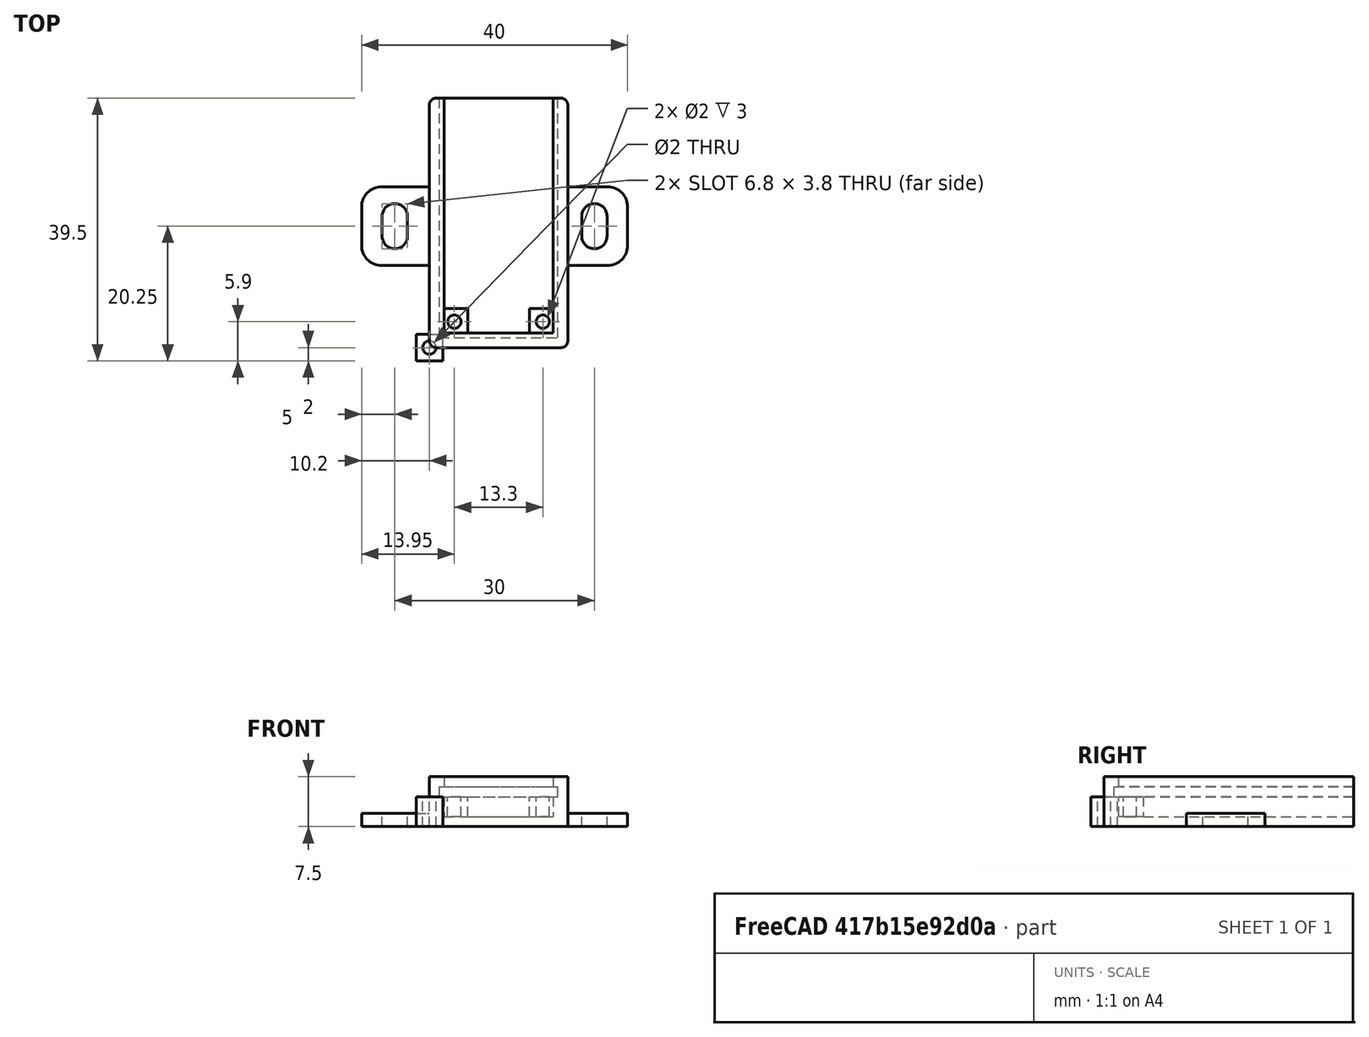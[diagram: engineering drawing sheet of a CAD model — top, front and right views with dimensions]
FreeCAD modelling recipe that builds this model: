
FCSTD DOCUMENT  (FreeCAD 0.19R23578 (Git))
Label: mosfet_d4184a_double
License: FreeArt
LicenseURL: http://artlibre.org/licence/lal
objects: Part::Box×4, Part::MultiFuse×3, Part::Cut×2, Spreadsheet::Sheet×1, Part::Fillet×1, Part::Feature×1, Part::Cylinder×1, Part::FeaturePython×1, App::Part×1
note: 12 computed .brp shape members not serialized (recipe doc carries the construction recipe); baked Part::Feature solids carry a one-line shape summary decoded from their .brp

FEATURE [Spreadsheet::Sheet] Spreadsheet  label="p"
  cells = A1=pcb_x; B1(pcb_x)=17.8; A2=pcb_y; B2(pcb_y)=36; A3=pcb_z; B3(pcb_z)=1.5; A4=pcb_under; B4(pcb_under)=3; A5=side_wall; B5(side_wall)=1.5; A6=pcb_side_lane; B6(pcb_side_lane)=0.7; A7=bottom_wall; B7(bottom_wall)=1.5; A8=pcb_above; B8(pcb_above)=1.5; A9=hole_dist_x; B9(hole_dist_x)=13.3; A10=hole_r; B10(hole_r)=1; A11=hole_off_y; B11(hole_off_y)=1.7; A12=hole_stand_size; B12(hole_stand_size)=4
FEATURE [Part::Box] Box  label="external cube"
  AttacherType = Attacher::AttachEngine3D
  Height = 7.5
  Length = 20.8
  Width = 37.5
  expr: Height = <<p>>.bottom_wall + <<p>>.pcb_under + <<p>>.pcb_z + <<p>>.pcb_above
  expr: Width = <<p>>.pcb_y + <<p>>.side_wall
  expr: Length = <<p>>.pcb_x + 2 * <<p>>.side_wall
FEATURE [Part::Box] Box006  label="internal cube"
  AttacherType = Attacher::AttachEngine3D
  Height = 6
  Length = 16.4
  Placement = pos=(2.2,2.2,1.5) rot=(0,0,1;0rad)
  Width = 36.1
  expr: .Placement.Base.y = <<p>>.side_wall + <<p>>.pcb_side_lane
  expr: .Placement.Base.x = <<p>>.side_wall + <<p>>.pcb_side_lane
  expr: .Placement.Base.z = <<p>>.bottom_wall
  expr: Height = <<p>>.pcb_under + <<p>>.pcb_z + <<p>>.pcb_above
  expr: Width = <<p>>.pcb_y - 2 * <<p>>.pcb_side_lane + <<p>>.side_wall
  expr: Length = <<p>>.pcb_x - 2 * <<p>>.pcb_side_lane
FEATURE [Part::Box] Box007  label="pcb extract cube"
  AttacherType = Attacher::AttachEngine3D
  Height = 1.5
  Length = 17.8
  Placement = pos=(1.5,1.5,4.5) rot=(0,0,1;0rad)
  Width = 36
  expr: .Placement.Base.y = <<p>>.side_wall
  expr: .Placement.Base.x = <<p>>.side_wall
  expr: Length = <<p>>.pcb_x
  expr: Width = <<p>>.pcb_y
  expr: .Placement.Base.z = <<p>>.bottom_wall + <<p>>.pcb_under
  expr: Height = <<p>>.pcb_z
FEATURE [Part::MultiFuse] Fusion  label="extract fusion"
  Shapes = -> [Box006,Box007]
FEATURE [Part::Fillet] Fillet  label="external fillet"
  Base = -> Box
  Edges = 4 edges r=1: [Edge1,Edge3,Edge5,Edge7]
FEATURE [Part::Feature] Cut003001  label="attach plane x dir001"
  Placement = pos=(-10.2,12.35,0) rot=(0,0,1;0rad)
  shape: bbox 40 x 11.8 x 2 mm, 18 faces (baked)
FEATURE [Part::MultiFuse] Fusion001  label="body fusion"
  Shapes = -> [Fillet,Cut003001]
FEATURE [Part::Cut] Cut  label="d4184a cut"
  Base = -> Fusion001
  Tool = -> Fusion
FEATURE [Part::Cylinder] Cylinder  label="hole"
  Angle = 360
  AttacherType = Attacher::AttachEngine3D
  Height = 10
  Radius = 1
  expr: Radius = <<p>>.hole_r
FEATURE [Part::Box] Box008  label="stand"
  AttacherType = Attacher::AttachEngine3D
  Height = 4.5
  Length = 4
  Placement = pos=(-2,-2,0) rot=(0,0,1;0rad)
  Width = 4
  expr: Height = <<p>>.pcb_under + <<p>>.bottom_wall
  expr: Length = <<p>>.hole_stand_size
  expr: Width = <<p>>.hole_stand_size
  expr: .Placement.Base.x = -<<p>>.hole_stand_size / 2
  expr: .Placement.Base.y = -<<p>>.hole_stand_size / 2
FEATURE [Part::Cut] Cut003002  label="stand hole cut"
  Base = -> Box008
  Tool = -> Cylinder
FEATURE [Part::FeaturePython] Array  label="hole array"  # Draft array (typed FeaturePython)
  Angle = 360
  ArrayType = 0
  Axis = (0,0,1)
  Base = -> Cut003002
  Center = (0,0,0)
  Count = 2
  ExpandArray = false
  Fuse = false
  IntervalAxis = (0,0,0)
  IntervalX = (13.3,0,0)
  IntervalY = (0,100,0)
  IntervalZ = (0,0,100)
  NumberCircles = 3
  NumberPolar = 5
  NumberX = 2
  NumberY = 1
  NumberZ = 1
  Placement = pos=(3.75,3.9,0) rot=(0,0,1;0rad)
  PlacementList = 2 placements: [(0,0,0),(13.3,0,0)]
  RadialDistance = 50
  ScaleList = (2) [(1,1,1),(1,1,1)]
  Symmetry = 1
  TangentialDistance = 25
  expr: .IntervalX.x = <<p>>.hole_dist_x
  expr: .Placement.Base.y = <<p>>.hole_off_y + <<p>>.side_wall + <<p>>.pcb_side_lane
  expr: .Placement.Base.x = (2 * <<p>>.side_wall + <<p>>.pcb_x - <<p>>.hole_dist_x) / 2
FEATURE [Part::MultiFuse] Fusion002  label="d4184a fusion"
  Shapes = -> [Array,Cut]
FEATURE [App::Part] Part  label="d4184a pcb box part"
  Group = -> [Box,Fillet,Fusion001,Fusion,Box007,Box006,Cut,Cylinder,Box008,Cut003001,Cut003002,Array,Fusion002]
  Origin = -> Origin
